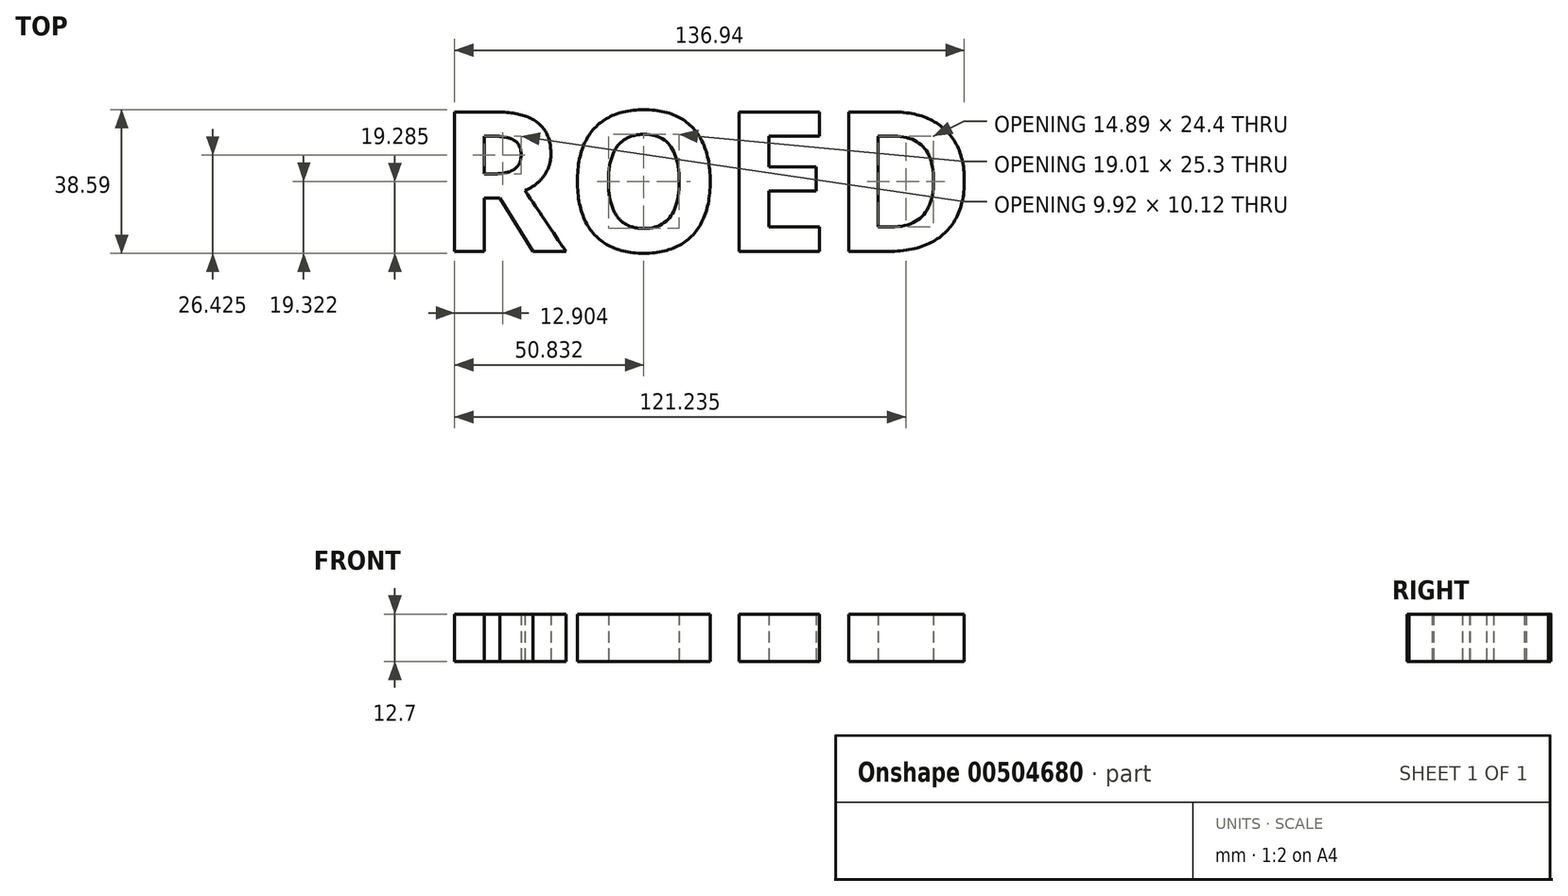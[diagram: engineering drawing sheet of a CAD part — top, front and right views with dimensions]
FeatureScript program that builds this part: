
annotation { "Feature Type Name" : "Feature", "Feature Type Description" : "" }
export const myFeature = defineFeature(function(context is Context, id is Id, definition is map)
    precondition{}
    {
        {
            var Q0;
            Q0=qCreatedBy(makeId("Top.planeOp"),FACE);
            var sketch = newSketch(context, id + "F0", { "sketchPlane" : qUnion([Q0])});
            skText(sketch, "E0", { "text": "ROED", "fontName": "OpenSans-Bold.ttf"});
            const initialGuessF0  = {"E0": [-0.05399, -0.0459, 1, 0, 0.0378]};
            skSetInitialGuess(sketch, initialGuessF0);
            skSolve(sketch);
        }
        {
            var Q0;
            Q0 = qSketchRegion(id + "F0", true);
            extrude(context, id + "F1", {"entities" : qUnion([Q0]), "depth" : 12.7 * mm});
        }
    });
